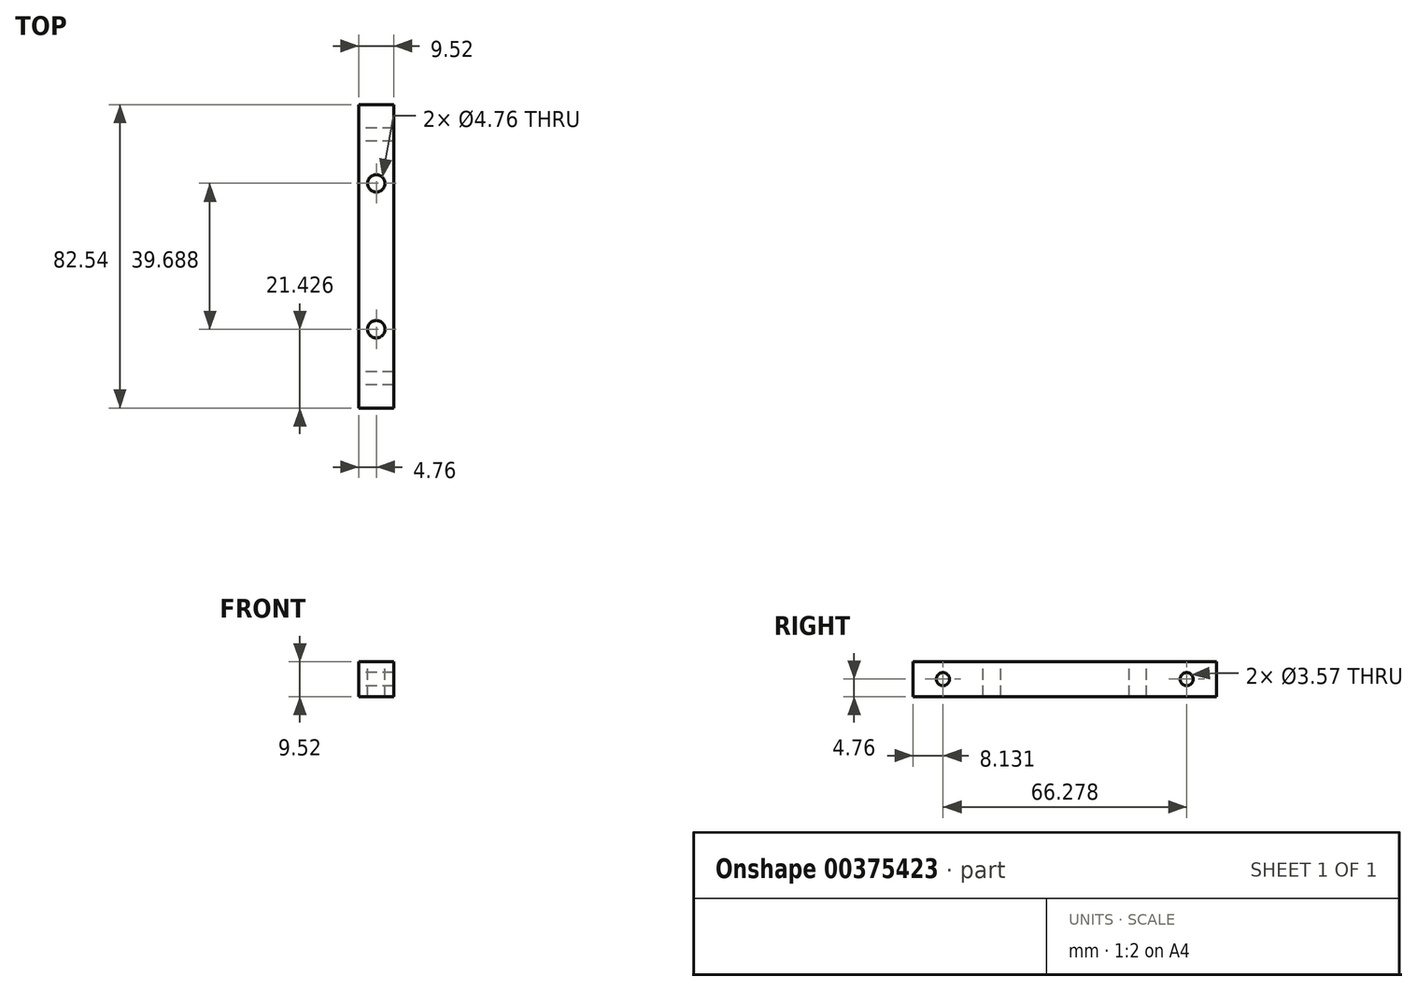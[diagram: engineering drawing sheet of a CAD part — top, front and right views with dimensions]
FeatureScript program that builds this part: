
annotation { "Feature Type Name" : "Feature", "Feature Type Description" : "" }
export const myFeature = defineFeature(function(context is Context, id is Id, definition is map)
    precondition{}
    {
        {
            var Q0;
            Q0=qCreatedBy(makeId("Front.planeOp"),FACE);
            var sketch = newSketch(context, id + "F0", { "sketchPlane" : qUnion([Q0])});
            skLineSegment(sketch, "E0.bottom", {"start": v(4.76, 4.76) * mm, "end": v(-4.76, 4.76) * mm});
            skLineSegment(sketch, "E0.top", {"start": v(4.76, -4.76) * mm, "end": v(-4.76, -4.76) * mm});
            skLineSegment(sketch, "E0.left", {"start": v(4.76, 4.76) * mm, "end": v(4.76, -4.76) * mm});
            skLineSegment(sketch, "E0.right", {"start": v(-4.76, 4.76) * mm, "end": v(-4.76, -4.76) * mm});
            skPoint(sketch, "E0.middle", {"position": v(0, 0) * mm});
            skSolve(sketch);
        }
        {
            var Q0;
            Q0=qSketchRegion(id+"F0",true);
            extrude(context, id + "F1", {"entities" : qUnion([Q0]), "depth" : 82.55 * mm, "symmetric" : true});
        }
        {
            var Q0;
            Q0=makeQuery(id+"F1.opExtrude","SWEPT_FACE",FACE,{"disambiguationData":[OSD([sQuery(id+"F0.wireOp",EDGE,"E0.right")])]});
            var sketch = newSketch(context, id + "F2", { "sketchPlane" : qUnion([Q0])});
            skCircle(sketch, "E1", {"center": v(-33.14, 0) * mm, "radius": 1.79 * mm});
            skCircle(sketch, "E2", {"center": v(33.14, 0) * mm, "radius": 1.79 * mm});
            skSolve(sketch);
        }
        {
            var Q0;
            Q0=qSketchRegion(id+"F2",true);
            extrude(context, id + "F3", {"entities" : qUnion([Q0]), "operationType" : NewBodyOperationType.REMOVE, "endBound" : BoundingType.THROUGH_ALL, "oppositeDirection" : true, "depth" : 25.4 * mm});
        }
        {
            var Q0;
            Q0=makeQuery(id+"F1.opExtrude","SWEPT_FACE",FACE,{"disambiguationData":[OSD([sQuery(id+"F0.wireOp",EDGE,"E0.bottom")])]});
            var sketch = newSketch(context, id + "F4", { "sketchPlane" : qUnion([Q0])});
            skCircle(sketch, "E3", {"center": v(0, 19.84) * mm, "radius": 2.38 * mm});
            skCircle(sketch, "E4", {"center": v(0, -19.84) * mm, "radius": 2.38 * mm});
            skSolve(sketch);
        }
        {
            var Q0;
            Q0=qSketchRegion(id+"F4",true);
            extrude(context, id + "F5", {"entities" : qUnion([Q0]), "operationType" : NewBodyOperationType.REMOVE, "endBound" : BoundingType.THROUGH_ALL, "oppositeDirection" : true, "depth" : 25.4 * mm});
        }
    });
